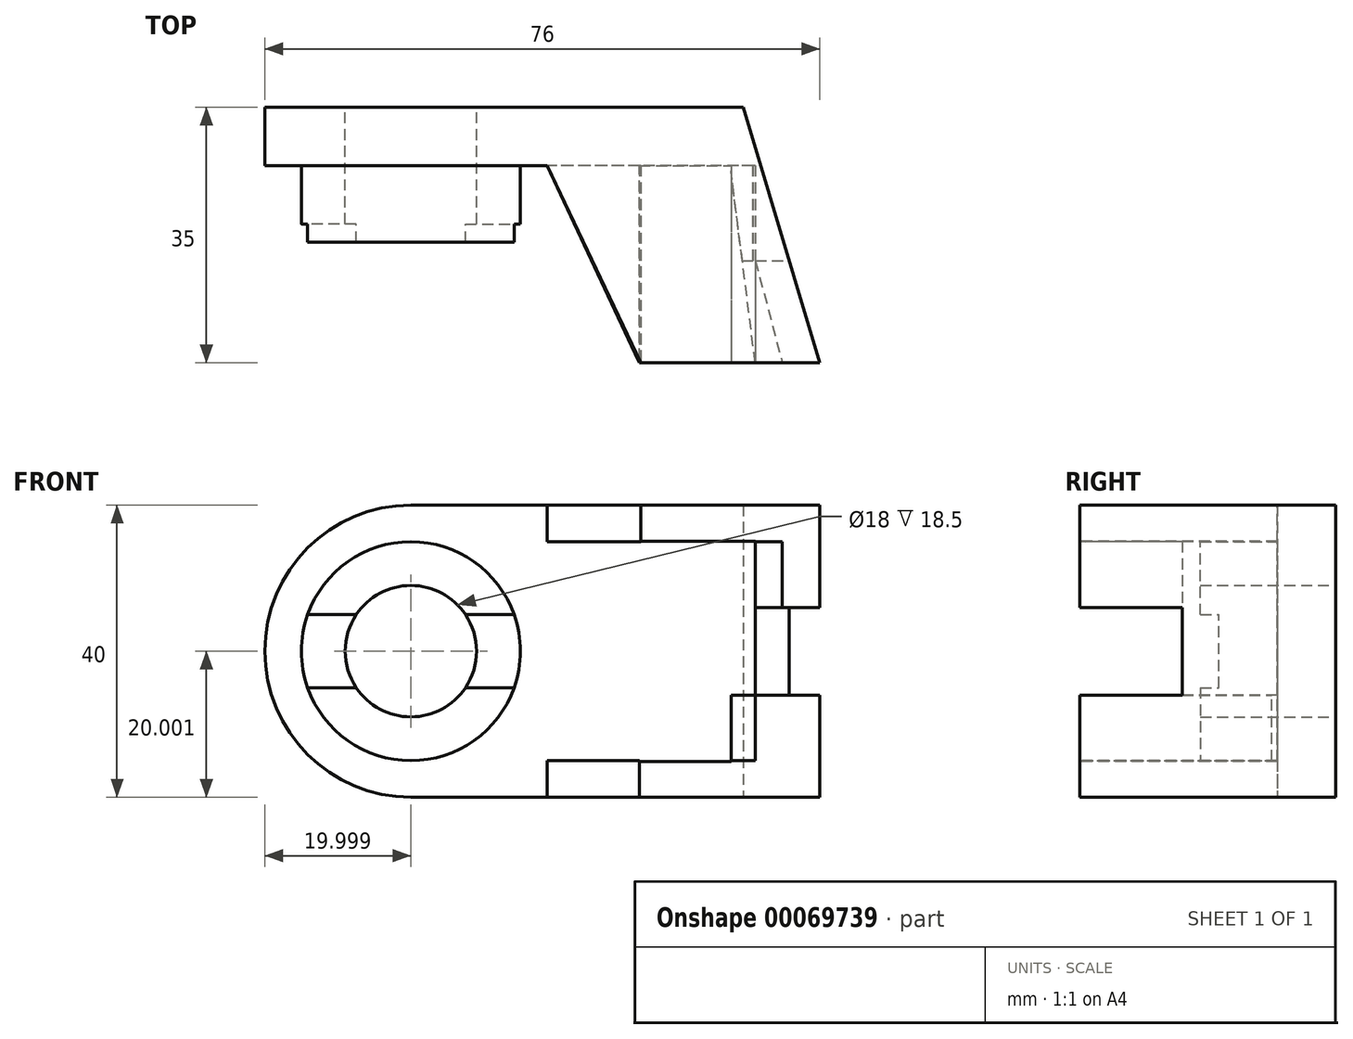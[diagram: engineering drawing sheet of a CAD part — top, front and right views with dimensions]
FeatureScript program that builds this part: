
annotation { "Feature Type Name" : "Feature", "Feature Type Description" : "" }
export const myFeature = defineFeature(function(context is Context, id is Id, definition is map)
    precondition{}
    {
        {
            var Q0;
            Q0=qCreatedBy(makeId("Front.planeOp"),FACE);
            var sketch = newSketch(context, id + "F0", { "sketchPlane" : qUnion([Q0])});
            skCircle(sketch, "E0", {"center": v(12.52, -39.27) * mm, "radius": 9 * mm});
            skLineSegment(sketch, "E1", {"start": v(12.52, -59.27) * mm, "end": v(68.52, -59.27) * mm});
            skLineSegment(sketch, "E2", {"start": v(68.52, -59.27) * mm, "end": v(68.52, -45.27) * mm});
            skLineSegment(sketch, "E3", {"start": v(5.04, -34.27) * mm, "end": v(-1.62, -34.27) * mm});
            skCircle(sketch, "E4", {"center": v(12.52, -39.27) * mm, "radius": 15 * mm});
            skLineSegment(sketch, "E5", {"start": v(20, -34.27) * mm, "end": v(26.66, -34.27) * mm});
            skLineSegment(sketch, "E6", {"start": v(68.52, -19.27) * mm, "end": v(68.52, -33.27) * mm});
            skLineSegment(sketch, "E7", {"start": v(5.04, -44.27) * mm, "end": v(-1.62, -44.27) * mm});
            skLineSegment(sketch, "E8", {"start": v(12.52, -19.27) * mm, "end": v(68.52, -19.27) * mm});
            skLineSegment(sketch, "E9", {"start": v(20, -44.27) * mm, "end": v(26.66, -44.27) * mm});
            skArc(sketch, "E10", {"start": v(12.52, -19.27) * mm, "mid": v(-7.48, -39.27) * mm, "end": v(12.52, -59.27) * mm});
            skLineSegment(sketch, "E11", {"start": v(68.52, -33.27) * mm, "end": v(68.52, -45.27) * mm});
            skLineSegment(sketch, "E12", {"start": v(31.18, -19.27) * mm, "end": v(31.18, -24.27) * mm});
            skLineSegment(sketch, "E13", {"start": v(31.18, -59.27) * mm, "end": v(31.18, -54.27) * mm});
            skLineSegment(sketch, "E14", {"start": v(31.18, -54.27) * mm, "end": v(61.18, -54.27) * mm});
            skLineSegment(sketch, "E15", {"start": v(31.18, -24.27) * mm, "end": v(61.18, -24.27) * mm});
            skLineSegment(sketch, "E16", {"start": v(61.18, -24.27) * mm, "end": v(61.18, -54.27) * mm});
            skLineSegment(sketch, "E17", {"start": v(43.7, -24.27) * mm, "end": v(43.7, -54.27) * mm});
            skSolve(sketch);
        }
        {
            var Q0;
            {var subQ1=sQuery(id+"F0.wireOp",EDGE,"E10");Q0=makeQuery(id+"F0.imprint","IMPRINT",FACE,{"disambiguationData":[TD([[makeQuery(id+"F0.imprint","IMPRINT",EDGE,{"derivedFrom":subQ1}),1.0]])]});}
            var Q1;
            {var subQ0=sQuery(id+"F0.wireOp",EDGE,"E16");Q1=makeQuery(id+"F0.imprint","IMPRINT",FACE,{"disambiguationData":[TD([[makeQuery(id+"F0.imprint","IMPRINT",EDGE,{"derivedFrom":subQ0}),-1.0]])]});}
            var Q2;
            {var subQ9=sQuery(id+"F0.wireOp",EDGE,"E2");Q2=makeQuery(id+"F0.imprint","IMPRINT",FACE,{"disambiguationData":[TD([[makeQuery(id+"F0.imprint","IMPRINT",EDGE,{"derivedFrom":subQ9}),1.0]])]});}
            extrude(context, id + "F1", {"entities" : qUnion([Q0, Q1, Q2]), "depth" : 8 * mm});
        }
        {
            var Q0;
            {var subQ0=sQuery(id+"F0.wireOp",EDGE,"E3");Q0=makeQuery(id+"F0.imprint","IMPRINT",FACE,{"disambiguationData":[TD([[makeQuery(id+"F0.imprint","IMPRINT",EDGE,{"derivedFrom":subQ0}),1.0]])]});}
            var Q1;
            {var subQ0=sQuery(id+"F0.wireOp",EDGE,"E5");Q1=makeQuery(id+"F0.imprint","IMPRINT",FACE,{"disambiguationData":[TD([[makeQuery(id+"F0.imprint","IMPRINT",EDGE,{"derivedFrom":subQ0}),-1.0]])]});}
            extrude(context, id + "F2", {"entities" : qUnion([Q0, Q1]), "operationType" : NewBodyOperationType.ADD, "depth" : 16 * mm});
        }
        {
            var Q0;
            {var subQ0=sQuery(id+"F0.wireOp",EDGE,"E3");Q0=makeQuery(id+"F0.imprint","IMPRINT",FACE,{"disambiguationData":[TD([[makeQuery(id+"F0.imprint","IMPRINT",EDGE,{"derivedFrom":subQ0}),-1.0]])]});}
            var Q1;
            {var subQ0=sQuery(id+"F0.wireOp",EDGE,"E7");Q1=makeQuery(id+"F0.imprint","IMPRINT",FACE,{"disambiguationData":[TD([[makeQuery(id+"F0.imprint","IMPRINT",EDGE,{"derivedFrom":subQ0}),1.0]])]});}
            extrude(context, id + "F3", {"entities" : qUnion([Q0, Q1]), "operationType" : NewBodyOperationType.ADD, "depth" : 18.5 * mm});
        }
        {
            var Q0;
            {var subQ9=sQuery(id+"F0.wireOp",EDGE,"E2");Q0=makeQuery(id+"F0.imprint","IMPRINT",FACE,{"disambiguationData":[TD([[makeQuery(id+"F0.imprint","IMPRINT",EDGE,{"derivedFrom":subQ9}),1.0]])]});}
            var Q1;
            {var subQ0=sQuery(id+"F0.wireOp",EDGE,"E16");Q1=makeQuery(id+"F0.imprint","IMPRINT",FACE,{"disambiguationData":[TD([[makeQuery(id+"F0.imprint","IMPRINT",EDGE,{"derivedFrom":subQ0}),-1.0]])]});}
            extrude(context, id + "F4", {"entities" : qUnion([Q0, Q1]), "operationType" : NewBodyOperationType.ADD, "depth" : 35 * mm});
        }
        {
            var Q0;
            {var subQ0=sQuery(id+"F0.wireOp",EDGE,"E11");var subQ1=sQuery(id+"F0.wireOp",EDGE,"E6");var subQ2=sQuery(id+"F0.wireOp",EDGE,"E2");Q0=makeQuery(id+"F4.boolean.opBoolean","MERGE",FACE,{"derivedFrom":[makeQuery(id+"F1.opExtrude","SWEPT_FACE",FACE,{"disambiguationData":[OSD([subQ2,subQ1,subQ0])]}),makeQuery(id+"F4.opExtrude","SWEPT_FACE",FACE,{"disambiguationData":[OSD([subQ2,subQ1,subQ0])]})]});}
            var sketch = newSketch(context, id + "F5", { "sketchPlane" : qUnion([Q0])});
            skLineSegment(sketch, "E18", {"start": v(-35, -45.27) * mm, "end": v(-21, -45.27) * mm});
            skLineSegment(sketch, "E19", {"start": v(-21, -45.27) * mm, "end": v(-21, -33.27) * mm});
            skLineSegment(sketch, "E20", {"start": v(-21, -33.27) * mm, "end": v(-35, -33.27) * mm});
            skSolve(sketch);
        }
        {
            var Q0;
            {var subQ0=sQuery(id+"F5.wireOp",EDGE,"E18");Q0=makeQuery(id+"F5.imprint","IMPRINT",FACE,{"disambiguationData":[TD([[makeQuery(id+"F5.imprint","IMPRINT",EDGE,{"derivedFrom":subQ0}),1.0]])]});}
            extrude(context, id + "F6", {"entities" : qUnion([Q0]), "operationType" : NewBodyOperationType.REMOVE, "oppositeDirection" : true, "depth" : 35 * mm});
        }
        {
            var Q0;
            {var subQ0=sQuery(id+"F0.wireOp",EDGE,"E1");Q0=makeQuery(id+"F4.boolean.opBoolean","MERGE",FACE,{"derivedFrom":[makeQuery(id+"F1.opExtrude","SWEPT_FACE",FACE,{"disambiguationData":[OSD([subQ0])]}),makeQuery(id+"F4.opExtrude","SWEPT_FACE",FACE,{"disambiguationData":[OSD([subQ0])]})]});}
            var sketch = newSketch(context, id + "F7", { "sketchPlane" : qUnion([Q0])});
            skLineSegment(sketch, "E21", {"start": v(31.18, 8) * mm, "end": v(31.18, 35) * mm});
            skLineSegment(sketch, "E22", {"start": v(31.18, 35) * mm, "end": v(43.81, 35) * mm});
            skLineSegment(sketch, "E23", {"start": v(43.81, 35) * mm, "end": v(31.18, 8) * mm});
            skSolve(sketch);
        }
        {
            var Q0;
            Q0 = qSketchRegion(id + "F7", true);
            var Q1;
            Q1=makeQuery(id+"F7.imprint","IMPRINT",FACE,{"disambiguationData":[TD([[makeQuery(id+"F7.imprint","IMPRINT",EDGE,{"derivedFrom":sQuery(id+"F7.wireOp",EDGE,"E21")}),1.0]])]});
            extrude(context, id + "F8", {"entities" : qUnion([Q0, Q1]), "operationType" : NewBodyOperationType.REMOVE, "oppositeDirection" : true, "depth" : 25 * mm});
        }
        {
            var Q0;
            {var subQ0=sQuery(id+"F0.wireOp",EDGE,"E8");Q0=makeQuery(id+"F4.boolean.opBoolean","MERGE",FACE,{"derivedFrom":[makeQuery(id+"F1.opExtrude","SWEPT_FACE",FACE,{"disambiguationData":[OSD([subQ0])]}),makeQuery(id+"F4.opExtrude","SWEPT_FACE",FACE,{"disambiguationData":[OSD([subQ0])]})]});}
            var sketch = newSketch(context, id + "F9", { "sketchPlane" : qUnion([Q0])});
            skLineSegment(sketch, "E24", {"start": v(44.03, -35) * mm, "end": v(31.18, -35) * mm});
            skLineSegment(sketch, "E25", {"start": v(31.18, -35) * mm, "end": v(31.18, -8) * mm});
            skLineSegment(sketch, "E26", {"start": v(31.18, -8) * mm, "end": v(44.03, -35) * mm});
            skSolve(sketch);
        }
        {
            var Q0;
            Q0 = qSketchRegion(id + "F9", true);
            extrude(context, id + "F10", {"entities" : qUnion([Q0]), "operationType" : NewBodyOperationType.REMOVE, "oppositeDirection" : true, "depth" : 25 * mm});
        }
        {
            var Q0;
            {var subQ0=sQuery(id+"F0.wireOp",EDGE,"E1");Q0=makeQuery(id+"F4.boolean.opBoolean","MERGE",FACE,{"derivedFrom":[makeQuery(id+"F1.opExtrude","SWEPT_FACE",FACE,{"disambiguationData":[OSD([subQ0])]}),makeQuery(id+"F4.opExtrude","SWEPT_FACE",FACE,{"disambiguationData":[OSD([subQ0])]})]});}
            var sketch = newSketch(context, id + "F11", { "sketchPlane" : qUnion([Q0])});
            skLineSegment(sketch, "E27", {"start": v(68.52, 35) * mm, "end": v(68.52, 0) * mm});
            skLineSegment(sketch, "E28", {"start": v(68.52, 0) * mm, "end": v(58.03, 0) * mm});
            skLineSegment(sketch, "E29", {"start": v(58.03, 0) * mm, "end": v(68.52, 35) * mm});
            skSolve(sketch);
        }
        {
            var Q0;
            Q0 = qSketchRegion(id + "F11", true);
            extrude(context, id + "F12", {"entities" : qUnion([Q0]), "operationType" : NewBodyOperationType.REMOVE, "oppositeDirection" : true, "depth" : 45 * mm});
        }
        {
            var Q0;
            {var subQ0=sQuery(id+"F0.wireOp",EDGE,"E8");var subQ1=sQuery(id+"F0.wireOp",EDGE,"E11");var subQ2=sQuery(id+"F0.wireOp",EDGE,"E6");var subQ3=sQuery(id+"F0.wireOp",EDGE,"E2");var subQ4=sQuery(id+"F0.wireOp",EDGE,"E17");var subQ5=sQuery(id+"F0.wireOp",EDGE,"E12");var subQ6=sQuery(id+"F0.wireOp",EDGE,"E15");Q0=makeQuery(id+"F6.boolean.opBoolean","SPLIT",FACE,{"disambiguationData":[TD([makeQuery(id+"F1.opExtrude","SWEPT_FACE",FACE,{"disambiguationData":[OSD([subQ0])]})])],"derivedFrom":makeQuery(id+"F4.opExtrude","CAP_FACE",FACE,{"disambiguationData":[OSD([sQuery(id+"F0.wireOp",EDGE,"E1"),subQ3,subQ2,subQ0,subQ1,subQ5,sQuery(id+"F0.wireOp",EDGE,"E13"),sQuery(id+"F0.wireOp",EDGE,"E14"),subQ6,subQ4])],"isStart":false})});}
            var sketch = newSketch(context, id + "F13", { "sketchPlane" : qUnion([Q0])});
            skLineSegment(sketch, "E30", {"start": v(44.03, -33.27) * mm, "end": v(56.28, -33.27) * mm});
            skLineSegment(sketch, "E31", {"start": v(56.28, -33.27) * mm, "end": v(56.28, -24.23) * mm});
            skLineSegment(sketch, "E32", {"start": v(56.28, -24.23) * mm, "end": v(44.03, -24.23) * mm});
            skSolve(sketch);
        }
        {
            var Q0;
            {var subQ0=sQuery(id+"F13.wireOp",EDGE,"E30");Q0=makeQuery(id+"F13.imprint","IMPRINT",FACE,{"disambiguationData":[TD([[makeQuery(id+"F13.imprint","IMPRINT",EDGE,{"derivedFrom":subQ0}),1.0]])]});}
            extrude(context, id + "F14", {"entities" : qUnion([Q0]), "operationType" : NewBodyOperationType.REMOVE, "oppositeDirection" : true, "depth" : 27 * mm});
        }
        {
            var Q0;
            Q0=makeQuery(id+"F4.opExtrude","SWEPT_FACE",FACE,{"disambiguationData":[OSD([sQuery(id+"F0.wireOp",EDGE,"E17")])]});
            var sketch = newSketch(context, id + "F15", { "sketchPlane" : qUnion([Q0])});
            skLineSegment(sketch, "E33", {"start": v(34.3, -24.27) * mm, "end": v(8, -24.27) * mm});
            skLineSegment(sketch, "E34", {"start": v(34.3, -33.27) * mm, "end": v(8, -33.27) * mm});
            skLineSegment(sketch, "E35", {"start": v(8, -33.27) * mm, "end": v(8, -24.27) * mm});
            skLineSegment(sketch, "E36", {"start": v(34.3, -24.27) * mm, "end": v(34.3, -33.27) * mm});
            skSolve(sketch);
        }
        {
            var Q0;
            Q0 = qSketchRegion(id + "F15", true);
            extrude(context, id + "F16", {"entities" : qUnion([Q0]), "operationType" : NewBodyOperationType.REMOVE, "oppositeDirection" : true, "depth" : 5 * mm});
        }
        {
            var Q0;
            Q0=makeQuery(id+"F10.boolean.opBoolean","COPY",FACE,{"derivedFrom":makeQuery(id+"F10.opExtrude","SWEPT_FACE",FACE,{"disambiguationData":[OSD([sQuery(id+"F9.wireOp",EDGE,"E26")])]})});
            var sketch = newSketch(context, id + "F17", { "sketchPlane" : qUnion([Q0])});
            skLineSegment(sketch, "E37", {"start": v(49.74, -24.27) * mm, "end": v(50.53, -24.23) * mm});
            skLineSegment(sketch, "E38", {"start": v(50.53, -24.23) * mm, "end": v(50.53, -33.27) * mm});
            skLineSegment(sketch, "E39", {"start": v(50.53, -33.27) * mm, "end": v(49.74, -33.27) * mm});
            skLineSegment(sketch, "E40", {"start": v(49.74, -33.27) * mm, "end": v(49.74, -24.27) * mm});
            skSolve(sketch);
        }
        {
            var Q0;
            Q0 = qSketchRegion(id + "F17", true);
            extrude(context, id + "F18", {"entities" : qUnion([Q0]), "operationType" : NewBodyOperationType.REMOVE, "oppositeDirection" : true, "depth" : 5 * mm});
        }
        {
            var Q0;
            {var subQ0=sQuery(id+"F0.wireOp",EDGE,"E11");var subQ1=sQuery(id+"F0.wireOp",EDGE,"E6");var subQ2=sQuery(id+"F0.wireOp",EDGE,"E2");var subQ3=sQuery(id+"F0.wireOp",EDGE,"E13");var subQ4=sQuery(id+"F0.wireOp",EDGE,"E17");var subQ5=sQuery(id+"F0.wireOp",EDGE,"E1");var subQ6=sQuery(id+"F0.wireOp",EDGE,"E14");Q0=makeQuery(id+"F6.boolean.opBoolean","SPLIT",FACE,{"disambiguationData":[TD([makeQuery(id+"F1.opExtrude","SWEPT_FACE",FACE,{"disambiguationData":[OSD([subQ5])]})])],"derivedFrom":makeQuery(id+"F4.opExtrude","CAP_FACE",FACE,{"disambiguationData":[OSD([subQ5,subQ2,subQ1,sQuery(id+"F0.wireOp",EDGE,"E8"),subQ0,sQuery(id+"F0.wireOp",EDGE,"E12"),subQ3,subQ6,sQuery(id+"F0.wireOp",EDGE,"E15"),subQ4])],"isStart":false})});}
            var sketch = newSketch(context, id + "F19", { "sketchPlane" : qUnion([Q0])});
            skLineSegment(sketch, "E41", {"start": v(43.81, -45.27) * mm, "end": v(56.17, -45.27) * mm});
            skLineSegment(sketch, "E42", {"start": v(43.81, -45.27) * mm, "end": v(43.81, -54.37) * mm});
            skLineSegment(sketch, "E43", {"start": v(43.81, -54.37) * mm, "end": v(56.17, -54.37) * mm});
            skLineSegment(sketch, "E44", {"start": v(56.17, -54.37) * mm, "end": v(56.17, -45.27) * mm});
            skSolve(sketch);
        }
        {
            var Q0;
            Q0 = qSketchRegion(id + "F19", true);
            extrude(context, id + "F20", {"entities" : qUnion([Q0]), "operationType" : NewBodyOperationType.REMOVE, "oppositeDirection" : true, "depth" : 27 * mm});
        }
        {
            var Q0;
            Q0=makeQuery(id+"F8.boolean.opBoolean","COPY",FACE,{"derivedFrom":makeQuery(id+"F8.opExtrude","SWEPT_FACE",FACE,{"disambiguationData":[OSD([sQuery(id+"F7.wireOp",EDGE,"E23")])]})});
            var sketch = newSketch(context, id + "F21", { "sketchPlane" : qUnion([Q0])});
            skLineSegment(sketch, "E45", {"start": v(50.27, -45.27) * mm, "end": v(49.99, -45.27) * mm});
            skLineSegment(sketch, "E46", {"start": v(49.99, -45.27) * mm, "end": v(49.99, -54.27) * mm});
            skLineSegment(sketch, "E47", {"start": v(49.99, -54.27) * mm, "end": v(50.27, -54.37) * mm});
            skLineSegment(sketch, "E48", {"start": v(50.27, -54.37) * mm, "end": v(50.27, -45.27) * mm});
            skSolve(sketch);
        }
        {
            var Q0;
            Q0 = qSketchRegion(id + "F21", true);
            extrude(context, id + "F22", {"entities" : qUnion([Q0]), "operationType" : NewBodyOperationType.REMOVE, "oppositeDirection" : true, "depth" : 5 * mm});
        }
        {
            var Q0;
            Q0=makeQuery(id+"F4.opExtrude","SWEPT_FACE",FACE,{"disambiguationData":[OSD([sQuery(id+"F0.wireOp",EDGE,"E17")])]});
            var sketch = newSketch(context, id + "F23", { "sketchPlane" : qUnion([Q0])});
            skLineSegment(sketch, "E49", {"start": v(34.74, -45.27) * mm, "end": v(8, -45.27) * mm});
            skLineSegment(sketch, "E50", {"start": v(8, -45.27) * mm, "end": v(8, -54.27) * mm});
            skLineSegment(sketch, "E51", {"start": v(8, -54.27) * mm, "end": v(34.74, -54.27) * mm});
            skLineSegment(sketch, "E52", {"start": v(34.74, -54.27) * mm, "end": v(34.74, -45.27) * mm});
            skSolve(sketch);
        }
        {
            var Q0;
            Q0 = qSketchRegion(id + "F23", true);
            extrude(context, id + "F24", {"entities" : qUnion([Q0]), "operationType" : NewBodyOperationType.REMOVE, "oppositeDirection" : true, "depth" : 5 * mm});
        }
        {
            var Q0;
            Q0=makeQuery(id+"F6.boolean.opBoolean","COPY",FACE,{"derivedFrom":makeQuery(id+"F6.opExtrude","SWEPT_FACE",FACE,{"disambiguationData":[OSD([sQuery(id+"F5.wireOp",EDGE,"E19")])]})});
            var sketch = newSketch(context, id + "F25", { "sketchPlane" : qUnion([Q0])});
            skLineSegment(sketch, "E53", {"start": v(43.7, -45.27) * mm, "end": v(43.7, -33.27) * mm});
            skLineSegment(sketch, "E54", {"start": v(43.7, -33.27) * mm, "end": v(56.28, -33.27) * mm});
            skLineSegment(sketch, "E55", {"start": v(56.28, -33.27) * mm, "end": v(56.17, -45.27) * mm});
            skLineSegment(sketch, "E56", {"start": v(56.17, -45.27) * mm, "end": v(43.7, -45.27) * mm});
            skSolve(sketch);
        }
        {
            var Q0;
            Q0 = qSketchRegion(id + "F25", true);
            extrude(context, id + "F26", {"entities" : qUnion([Q0]), "operationType" : NewBodyOperationType.REMOVE, "oppositeDirection" : true, "depth" : 13 * mm});
        }
        {
            var Q0;
            Q0 = qSketchRegion(id + "F25", true);
            extrude(context, id + "F27", {"entities" : qUnion([Q0]), "operationType" : NewBodyOperationType.REMOVE, "oppositeDirection" : true, "depth" : 13 * mm});
        }
        {
            var Q0;
            {var subQ0=sQuery(id+"F0.wireOp",EDGE,"E11");var subQ1=sQuery(id+"F0.wireOp",EDGE,"E6");var subQ2=sQuery(id+"F0.wireOp",EDGE,"E2");var subQ3=sQuery(id+"F0.wireOp",EDGE,"E13");var subQ4=sQuery(id+"F0.wireOp",EDGE,"E17");var subQ5=sQuery(id+"F0.wireOp",EDGE,"E1");var subQ6=sQuery(id+"F0.wireOp",EDGE,"E14");Q0=makeQuery(id+"F6.boolean.opBoolean","SPLIT",FACE,{"disambiguationData":[TD([makeQuery(id+"F1.opExtrude","SWEPT_FACE",FACE,{"disambiguationData":[OSD([subQ5])]})])],"derivedFrom":makeQuery(id+"F4.opExtrude","CAP_FACE",FACE,{"disambiguationData":[OSD([subQ5,subQ2,subQ1,sQuery(id+"F0.wireOp",EDGE,"E8"),subQ0,sQuery(id+"F0.wireOp",EDGE,"E12"),subQ3,subQ6,sQuery(id+"F0.wireOp",EDGE,"E15"),subQ4])],"isStart":false})});}
            var sketch = newSketch(context, id + "F28", { "sketchPlane" : qUnion([Q0])});
            skLineSegment(sketch, "E57", {"start": v(56.17, -45.27) * mm, "end": v(62.34, -45.27) * mm});
            skLineSegment(sketch, "E58", {"start": v(62.34, -45.27) * mm, "end": v(56.95, -30.51) * mm});
            skLineSegment(sketch, "E59", {"start": v(56.95, -30.51) * mm, "end": v(56.17, -45.27) * mm});
            skSolve(sketch);
        }
        {
            var Q0;
            Q0 = qSketchRegion(id + "F28", true);
            extrude(context, id + "F29", {"entities" : qUnion([Q0]), "operationType" : NewBodyOperationType.REMOVE, "depth" : 9 * mm});
        }
        {
            var Q0;
            Q0 = qSketchRegion(id + "F25", true);
            extrude(context, id + "F30", {"entities" : qUnion([Q0]), "operationType" : NewBodyOperationType.REMOVE, "oppositeDirection" : true, "depth" : 13 * mm});
        }
        {
            var Q0;
            Q0=makeQuery(id+"F6.boolean.opBoolean","COPY",FACE,{"derivedFrom":makeQuery(id+"F6.opExtrude","SWEPT_FACE",FACE,{"disambiguationData":[OSD([sQuery(id+"F5.wireOp",EDGE,"E19")])]})});
            var sketch = newSketch(context, id + "F31", { "sketchPlane" : qUnion([Q0])});
            skLineSegment(sketch, "E60", {"start": v(56.28, -33.27) * mm, "end": v(64.32, -33.27) * mm});
            skLineSegment(sketch, "E61", {"start": v(64.32, -33.27) * mm, "end": v(64.32, -45.27) * mm});
            skLineSegment(sketch, "E62", {"start": v(64.32, -45.27) * mm, "end": v(56.17, -45.27) * mm});
            skLineSegment(sketch, "E63", {"start": v(56.17, -45.27) * mm, "end": v(56.28, -33.27) * mm});
            skSolve(sketch);
        }
        {
            var Q0;
            Q0=makeQuery(id+"F0vThq2afT1idHp_1.boolean.opBoolean","MERGE",FACE,{"derivedFrom":[makeQuery(id+"F14.boolean.opBoolean","SPLIT",FACE,{"disambiguationData":[TD([makeQuery(id+"F12.boolean.opBoolean","COPY",FACE,{"derivedFrom":makeQuery(id+"F12.opExtrude","SWEPT_FACE",FACE,{"disambiguationData":[OSD([sQuery(id+"F11.wireOp",EDGE,"E29")])]})})])],"derivedFrom":makeQuery(id+"F6.boolean.opBoolean","COPY",FACE,{"derivedFrom":makeQuery(id+"F6.opExtrude","SWEPT_FACE",FACE,{"disambiguationData":[OSD([sQuery(id+"F5.wireOp",EDGE,"E20")])]})})}),makeQuery(id+"F0vThq2afT1idHp_1.opExtrude","SWEPT_FACE",FACE,{"disambiguationData":[OSD([sQuery(id+"F31.wireOp",EDGE,"E60")])]})]});
            var sketch = newSketch(context, id + "F32", { "sketchPlane" : qUnion([Q0])});
            skLineSegment(sketch, "E64", {"start": v(56.28, 35) * mm, "end": v(56.28, 8) * mm});
            skLineSegment(sketch, "E65", {"start": v(56.28, 8) * mm, "end": v(63.4, 35) * mm});
            skLineSegment(sketch, "E66", {"start": v(63.4, 35) * mm, "end": v(56.28, 35) * mm});
            skSolve(sketch);
        }
        {
            var Q0;
            {var subQ0=sQuery(id+"F32.wireOp",EDGE,"E66");Q0=makeQuery(id+"F32.imprint","IMPRINT",FACE,{"disambiguationData":[TD([[makeQuery(id+"F32.imprint","IMPRINT",EDGE,{"derivedFrom":subQ0}),-1.0]])]});}
            extrude(context, id + "F33", {"entities" : qUnion([Q0]), "operationType" : NewBodyOperationType.REMOVE, "oppositeDirection" : true, "depth" : 9 * mm});
        }
        {
            var Q0;
            Q0=makeQuery(id+"F14.boolean.opBoolean","COPY",FACE,{"derivedFrom":makeQuery(id+"F14.opExtrude","SWEPT_FACE",FACE,{"disambiguationData":[OSD([sQuery(id+"F13.wireOp",EDGE,"E31")])]})});
            extrude(context, id + "F34", {"entities" : qUnion([Q0]), "operationType" : NewBodyOperationType.REMOVE, "oppositeDirection" : true, "depth" : 3.42 * mm});
        }
        {
            var Q0;
            Q0=makeQuery(id+"F34.boolean.opBoolean","COPY",FACE,{"derivedFrom":makeQuery(id+"F34.opExtrude","SWEPT_FACE",FACE,{"disambiguationData":[OSD([sQuery(id+"F0.wireOp",EDGE,"E2"),sQuery(id+"F0.wireOp",EDGE,"E6"),sQuery(id+"F0.wireOp",EDGE,"E11"),sQuery(id+"F5.wireOp",EDGE,"E19"),sQuery(id+"F5.wireOp",EDGE,"E20"),sQuery(id+"F13.wireOp",EDGE,"E30"),sQuery(id+"F13.wireOp",EDGE,"E31"),sQuery(id+"F25.wireOp",EDGE,"E54"),sQuery(id+"F25.wireOp",EDGE,"E55")])]})});
            extrude(context, id + "F35", {"entities" : qUnion([Q0]), "operationType" : NewBodyOperationType.REMOVE, "oppositeDirection" : true, "depth" : 12 * mm});
        }
        {
            var Q0;
            {var subQ0=sQuery(id+"F5.wireOp",EDGE,"E19");var subQ1=sQuery(id+"F0.wireOp",EDGE,"E11");var subQ2=sQuery(id+"F0.wireOp",EDGE,"E6");var subQ3=sQuery(id+"F0.wireOp",EDGE,"E2");Q0=makeQuery(id+"F35.boolean.opBoolean","MERGE",FACE,{"derivedFrom":[makeQuery(id+"F20.boolean.opBoolean","SPLIT",FACE,{"disambiguationData":[TD([makeQuery(id+"F12.boolean.opBoolean","COPY",FACE,{"derivedFrom":makeQuery(id+"F12.opExtrude","SWEPT_FACE",FACE,{"disambiguationData":[OSD([sQuery(id+"F11.wireOp",EDGE,"E29")])]})})])],"derivedFrom":makeQuery(id+"F6.boolean.opBoolean","COPY",FACE,{"derivedFrom":makeQuery(id+"F6.opExtrude","SWEPT_FACE",FACE,{"disambiguationData":[OSD([sQuery(id+"F5.wireOp",EDGE,"E18")])]})})}),makeQuery(id+"F35.opExtrude","CAP_FACE",FACE,{"disambiguationData":[OSD([subQ3,subQ2,subQ1,subQ0,sQuery(id+"F5.wireOp",EDGE,"E20"),sQuery(id+"F13.wireOp",EDGE,"E30"),sQuery(id+"F13.wireOp",EDGE,"E31"),sQuery(id+"F25.wireOp",EDGE,"E54"),sQuery(id+"F25.wireOp",EDGE,"E55")])],"isStart":false})]});}
            var sketch = newSketch(context, id + "F36", { "sketchPlane" : qUnion([Q0])});
            skLineSegment(sketch, "E67", {"start": v(56.17, -35) * mm, "end": v(59.7, -35) * mm});
            skLineSegment(sketch, "E68", {"start": v(59.7, -35) * mm, "end": v(56.28, -8) * mm});
            skLineSegment(sketch, "E69", {"start": v(56.28, -8) * mm, "end": v(56.17, -35) * mm});
            skSolve(sketch);
        }
        {
            var Q0;
            {var subQ12=sQuery(id+"F36.wireOp",EDGE,"E67");Q0=makeQuery(id+"F36.imprint","IMPRINT",FACE,{"disambiguationData":[TD([[makeQuery(id+"F36.imprint","IMPRINT",EDGE,{"derivedFrom":subQ12}),1.0]])]});}
            extrude(context, id + "F37", {"entities" : qUnion([Q0]), "operationType" : NewBodyOperationType.REMOVE, "oppositeDirection" : true, "depth" : 9 * mm});
        }
        {
            var Q0;
            Q0=makeQuery(id+"F20.boolean.opBoolean","COPY",FACE,{"derivedFrom":makeQuery(id+"F20.opExtrude","SWEPT_FACE",FACE,{"disambiguationData":[OSD([sQuery(id+"F19.wireOp",EDGE,"E44")])]})});
            var sketch = newSketch(context, id + "F38", { "sketchPlane" : qUnion([Q0])});
            skSolve(sketch);
        }
        {
            var Q0;
            {var subQ1=sQuery(id+"F19.wireOp",EDGE,"E44");Q0=makeQuery(id+"F38.imprint","IMPRINT",FACE,{"disambiguationData":[TD([[makeQuery(id+"F38.imprint","IMPRINT",EDGE,{"derivedFrom":makeQuery(id+"F20.boolean.opBoolean","COPY",EDGE,{"derivedFrom":makeQuery(id+"F20.opExtrude","CAP_EDGE",EDGE,{"disambiguationData":[OSD([subQ1])],"isStart":false})})}),-1.0]])]});}
            extrude(context, id + "F39", {"entities" : qUnion([Q0]), "operationType" : NewBodyOperationType.REMOVE, "oppositeDirection" : true, "depth" : 0.1 * mm});
        }
        {
            var Q0;
            Q0=makeQuery(id+"F39.boolean.opBoolean","COPY",FACE,{"derivedFrom":makeQuery(id+"F39.opExtrude","CAP_FACE",FACE,{"disambiguationData":[OSD([sQuery(id+"F0.wireOp",EDGE,"E2"),sQuery(id+"F0.wireOp",EDGE,"E6"),sQuery(id+"F0.wireOp",EDGE,"E11"),sQuery(id+"F5.wireOp",EDGE,"E18"),sQuery(id+"F5.wireOp",EDGE,"E19"),sQuery(id+"F19.wireOp",EDGE,"E41"),sQuery(id+"F19.wireOp",EDGE,"E43"),sQuery(id+"F19.wireOp",EDGE,"E44"),sQuery(id+"F25.wireOp",EDGE,"E55"),sQuery(id+"F25.wireOp",EDGE,"E56"),sQuery(id+"F36.wireOp",EDGE,"E67"),sQuery(id+"F36.wireOp",EDGE,"E69")])],"isStart":false})});
            extrude(context, id + "F40", {"entities" : qUnion([Q0]), "operationType" : NewBodyOperationType.REMOVE, "oppositeDirection" : true, "depth" : 0.1 * mm});
        }
        {
            var Q0;
            Q0=makeQuery(id+"F26.boolean.opBoolean","COPY",FACE,{"derivedFrom":makeQuery(id+"F26.opExtrude","SWEPT_FACE",FACE,{"disambiguationData":[OSD([sQuery(id+"F25.wireOp",EDGE,"E55")])]})});
            extrude(context, id + "F41", {"entities" : qUnion([Q0]), "operationType" : NewBodyOperationType.REMOVE, "oppositeDirection" : true, "depth" : 3.2 * mm});
        }
    });
